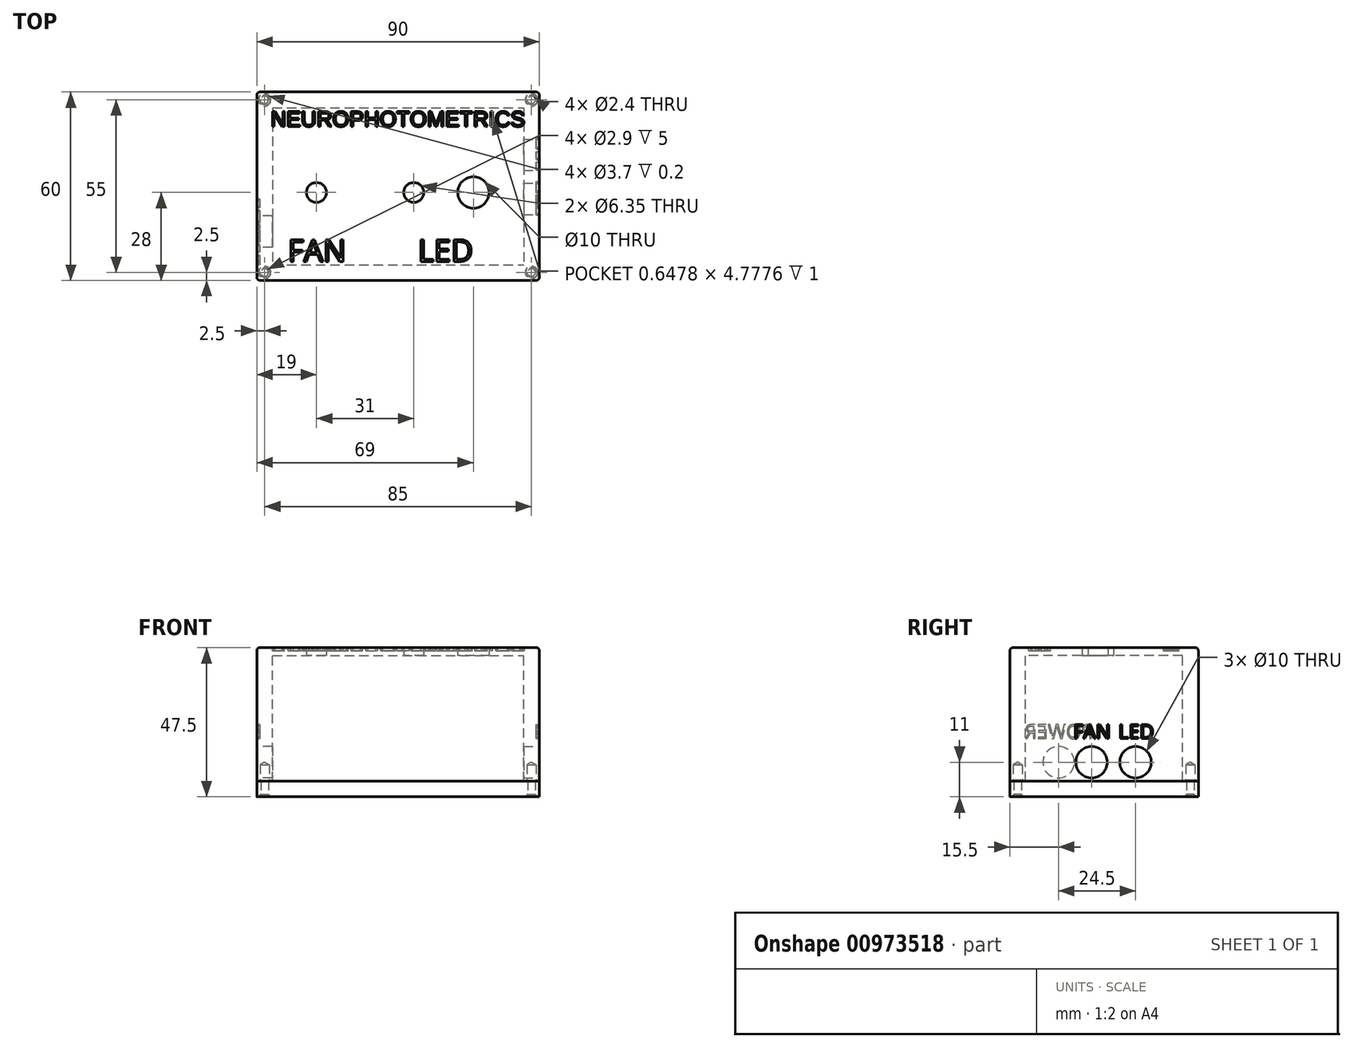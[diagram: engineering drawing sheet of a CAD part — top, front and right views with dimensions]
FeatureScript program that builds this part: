
annotation { "Feature Type Name" : "Feature", "Feature Type Description" : "" }
export const myFeature = defineFeature(function(context is Context, id is Id, definition is map)
    precondition{}
    {
        {
            var Q0;
            Q0=qCreatedBy(makeId("Top.planeOp"),FACE);
            var sketch = newSketch(context, id + "F0", { "sketchPlane" : qUnion([Q0])});
            skLineSegment(sketch, "E0.bottom", {"start": v(0, 0) * mm, "end": v(90, 0) * mm});
            skLineSegment(sketch, "E0.top", {"start": v(0, 60) * mm, "end": v(90, 60) * mm});
            skLineSegment(sketch, "E0.left", {"start": v(0, 0) * mm, "end": v(0, 60) * mm});
            skLineSegment(sketch, "E0.right", {"start": v(90, 0) * mm, "end": v(90, 60) * mm});
            skCircle(sketch, "E1", {"center": v(69, 28) * mm, "radius": 5 * mm});
            skCircle(sketch, "E2", {"center": v(19, 28) * mm, "radius": 3.18 * mm});
            skLineSegment(sketch, "E3", {"start": v(5, 60) * mm, "end": v(5, 5) * mm, "construction": true});
            skLineSegment(sketch, "E4", {"start": v(5, 5) * mm, "end": v(85, 5) * mm, "construction": true});
            skLineSegment(sketch, "E5", {"start": v(85, 5) * mm, "end": v(85, 60) * mm, "construction": true});
            skLineSegment(sketch, "E6", {"start": v(0, 55) * mm, "end": v(90, 55) * mm, "construction": true});
            skLineSegment(sketch, "E7", {"start": v(5, 5) * mm, "end": v(0, 5) * mm, "construction": true});
            skLineSegment(sketch, "E8", {"start": v(85, 5) * mm, "end": v(90, 5) * mm, "construction": true});
            skPoint(sketch, "E9.endSnap0", {"position": v(5, 32.5) * mm});
            skLineSegment(sketch, "E10", {"start": v(5, 60) * mm, "end": v(85, 55) * mm, "construction": true});
            skLineSegment(sketch, "E11", {"start": v(85, 60) * mm, "end": v(5, 55) * mm, "construction": true});
            skLineSegment(sketch, "E12", {"start": v(90, 5) * mm, "end": v(0, 0) * mm, "construction": true});
            skLineSegment(sketch, "E13", {"start": v(0, 5) * mm, "end": v(90, 0) * mm, "construction": true});
            skPoint(sketch, "E14", {"position": v(45, 2.5) * mm});
            skPoint(sketch, "E15", {"position": v(45, 57.5) * mm});
            skLineSegment(sketch, "E16", {"start": v(5, 28) * mm, "end": v(85, 28) * mm, "construction": true});
            skCircle(sketch, "E17", {"center": v(50, 28) * mm, "radius": 3.18 * mm});
            skSolve(sketch);
        }
        {
            var Q0;
            Q0=makeQuery(id+"F0.imprint","IMPRINT",FACE,{"disambiguationData":[TD([[makeQuery(id+"F0.imprint","IMPRINT",EDGE,{"derivedFrom":sQuery(id+"F0.wireOp",EDGE,"E0.bottom")}),1.0]])]});
            extrude(context, id + "F1", {"entities" : qUnion([Q0]), "depth" : 2.5 * mm, "offsetDistance" : 25 * mm});
        }
        {
            var Q0;
            Q0=makeQuery(id+"F1.opExtrude","CAP_FACE",FACE,{"disambiguationData":[OSD([sQuery(id+"F0.wireOp",EDGE,"E0.bottom"),sQuery(id+"F0.wireOp",EDGE,"E0.top"),sQuery(id+"F0.wireOp",EDGE,"E0.left"),sQuery(id+"F0.wireOp",EDGE,"E0.right"),sQuery(id+"F0.wireOp",EDGE,"692mbZP9-ke58-QfXx-eCDH-dWQCKjaEO8YG"),sQuery(id+"F0.wireOp",EDGE,"E1"),sQuery(id+"F0.wireOp",EDGE,"E2")])],"isStart":true});
            var sketch = newSketch(context, id + "F2", { "sketchPlane" : qUnion([Q0])});
            skLineSegment(sketch, "E18.bottom", {"start": v(0, -60) * mm, "end": v(90, -60) * mm, "construction": true});
            skLineSegment(sketch, "E18.top", {"start": v(0, 0) * mm, "end": v(90, 0) * mm, "construction": true});
            skLineSegment(sketch, "E18.left", {"start": v(0, -60) * mm, "end": v(0, 0) * mm, "construction": true});
            skLineSegment(sketch, "E18.right", {"start": v(90, -60) * mm, "end": v(90, 0) * mm, "construction": true});
            skLineSegment(sketch, "E19.bottom", {"start": v(5, -55) * mm, "end": v(85, -55) * mm});
            skLineSegment(sketch, "E19.top", {"start": v(5, -5) * mm, "end": v(85, -5) * mm});
            skLineSegment(sketch, "E19.left", {"start": v(5, -55) * mm, "end": v(5, -5) * mm});
            skLineSegment(sketch, "E19.right", {"start": v(85, -55) * mm, "end": v(85, -5) * mm});
            skSolve(sketch);
        }
        {
            var Q0;
            Q0=makeQuery(id+"F2.imprint","IMPRINT",FACE,{"disambiguationData":[TD([[makeQuery(id+"F2.imprint","IMPRINT",EDGE,{"derivedFrom":sQuery(id+"F2.wireOp",EDGE,"E19.bottom")}),-1.0]])]});
            var Q1;
            Q1=makeQuery(id+"F2.imprint","IMPRINT",FACE,{"disambiguationData":[TD([[makeQuery(id+"F2.imprint","IMPRINT",EDGE,{"derivedFrom":makeQuery(id+"FxvTJw6m9mzOm3c_1.hole-0.boolean.opBoolean","INTERSECT",EDGE,{"derivedFrom":[makeQuery(id+"F1.opExtrude","CAP_FACE",FACE,{"disambiguationData":[OSD([sQuery(id+"F0.wireOp",EDGE,"E0.bottom"),sQuery(id+"F0.wireOp",EDGE,"E0.top"),sQuery(id+"F0.wireOp",EDGE,"E0.left"),sQuery(id+"F0.wireOp",EDGE,"E0.right"),sQuery(id+"F0.wireOp",EDGE,"692mbZP9-ke58-QfXx-eCDH-dWQCKjaEO8YG"),sQuery(id+"F0.wireOp",EDGE,"E1"),sQuery(id+"F0.wireOp",EDGE,"E2")])],"isStart":true}),makeQuery(id+"FxvTJw6m9mzOm3c_1.hole-0.opRevolve","SWEPT_FACE",FACE,{"disambiguationData":[OSD([sQuery(id+"FxvTJw6m9mzOm3c_1.hole-0.sketch.wireOp",EDGE,"core_line_2")])]})]})}),1.0]])]});
            var Q2;
            Q2=makeQuery(id+"F2.imprint","IMPRINT",FACE,{"disambiguationData":[TD([[makeQuery(id+"F2.imprint","IMPRINT",EDGE,{"derivedFrom":makeQuery(id+"FxvTJw6m9mzOm3c_1.hole-1.boolean.opBoolean","INTERSECT",EDGE,{"derivedFrom":[makeQuery(id+"F1.opExtrude","CAP_FACE",FACE,{"disambiguationData":[OSD([sQuery(id+"F0.wireOp",EDGE,"E0.bottom"),sQuery(id+"F0.wireOp",EDGE,"E0.top"),sQuery(id+"F0.wireOp",EDGE,"E0.left"),sQuery(id+"F0.wireOp",EDGE,"E0.right"),sQuery(id+"F0.wireOp",EDGE,"692mbZP9-ke58-QfXx-eCDH-dWQCKjaEO8YG"),sQuery(id+"F0.wireOp",EDGE,"E1"),sQuery(id+"F0.wireOp",EDGE,"E2")])],"isStart":true}),makeQuery(id+"FxvTJw6m9mzOm3c_1.hole-1.opRevolve","SWEPT_FACE",FACE,{"disambiguationData":[OSD([sQuery(id+"FxvTJw6m9mzOm3c_1.hole-1.sketch.wireOp",EDGE,"core_line_2")])]})]})}),1.0]])]});
            var Q3;
            Q3=makeQuery(id+"F2.imprint","IMPRINT",FACE,{"disambiguationData":[TD([[makeQuery(id+"F2.imprint","IMPRINT",EDGE,{"derivedFrom":makeQuery(id+"FxvTJw6m9mzOm3c_1.hole-2.boolean.opBoolean","INTERSECT",EDGE,{"derivedFrom":[makeQuery(id+"F1.opExtrude","CAP_FACE",FACE,{"disambiguationData":[OSD([sQuery(id+"F0.wireOp",EDGE,"E0.bottom"),sQuery(id+"F0.wireOp",EDGE,"E0.top"),sQuery(id+"F0.wireOp",EDGE,"E0.left"),sQuery(id+"F0.wireOp",EDGE,"E0.right"),sQuery(id+"F0.wireOp",EDGE,"692mbZP9-ke58-QfXx-eCDH-dWQCKjaEO8YG"),sQuery(id+"F0.wireOp",EDGE,"E1"),sQuery(id+"F0.wireOp",EDGE,"E2")])],"isStart":true}),makeQuery(id+"FxvTJw6m9mzOm3c_1.hole-2.opRevolve","SWEPT_FACE",FACE,{"disambiguationData":[OSD([sQuery(id+"FxvTJw6m9mzOm3c_1.hole-2.sketch.wireOp",EDGE,"core_line_2")])]})]})}),1.0]])]});
            var Q4;
            Q4=makeQuery(id+"F2.imprint","IMPRINT",FACE,{"disambiguationData":[TD([[makeQuery(id+"F2.imprint","IMPRINT",EDGE,{"derivedFrom":makeQuery(id+"FxvTJw6m9mzOm3c_1.hole-3.boolean.opBoolean","INTERSECT",EDGE,{"derivedFrom":[makeQuery(id+"F1.opExtrude","CAP_FACE",FACE,{"disambiguationData":[OSD([sQuery(id+"F0.wireOp",EDGE,"E0.bottom"),sQuery(id+"F0.wireOp",EDGE,"E0.top"),sQuery(id+"F0.wireOp",EDGE,"E0.left"),sQuery(id+"F0.wireOp",EDGE,"E0.right"),sQuery(id+"F0.wireOp",EDGE,"692mbZP9-ke58-QfXx-eCDH-dWQCKjaEO8YG"),sQuery(id+"F0.wireOp",EDGE,"E1"),sQuery(id+"F0.wireOp",EDGE,"E2")])],"isStart":true}),makeQuery(id+"FxvTJw6m9mzOm3c_1.hole-3.opRevolve","SWEPT_FACE",FACE,{"disambiguationData":[OSD([sQuery(id+"FxvTJw6m9mzOm3c_1.hole-3.sketch.wireOp",EDGE,"core_line_2")])]})]})}),1.0]])]});
            extrude(context, id + "F3", {"entities" : qUnion([Q0, Q1, Q2, Q3, Q4]), "depth" : 40 * mm, "offsetDistance" : 25 * mm});
        }
        {
            var Q0;
            Q0=makeQuery(id+"F3.opExtrude","CAP_FACE",FACE,{"disambiguationData":[OSD([sQuery(id+"F0.wireOp",EDGE,"E0.bottom"),sQuery(id+"F0.wireOp",EDGE,"E0.top"),sQuery(id+"F0.wireOp",EDGE,"E0.left"),sQuery(id+"F0.wireOp",EDGE,"E0.right"),sQuery(id+"F2.wireOp",EDGE,"E19.bottom"),sQuery(id+"F2.wireOp",EDGE,"E19.top"),sQuery(id+"F2.wireOp",EDGE,"E19.left"),sQuery(id+"F2.wireOp",EDGE,"E19.right")])],"isStart":false});
            var sketch = newSketch(context, id + "F4", { "sketchPlane" : qUnion([Q0])});
            skLineSegment(sketch, "E20.bottom", {"start": v(0, 0) * mm, "end": v(90, 0) * mm});
            skLineSegment(sketch, "E20.top", {"start": v(0, -60) * mm, "end": v(90, -60) * mm});
            skLineSegment(sketch, "E20.left", {"start": v(0, 0) * mm, "end": v(0, -60) * mm});
            skLineSegment(sketch, "E20.right", {"start": v(90, 0) * mm, "end": v(90, -60) * mm});
            skLineSegment(sketch, "E21.bottom", {"start": v(5, -5) * mm, "end": v(85, -5) * mm, "construction": true});
            skLineSegment(sketch, "E21.top", {"start": v(5, -55) * mm, "end": v(85, -55) * mm, "construction": true});
            skLineSegment(sketch, "E21.left", {"start": v(5, -5) * mm, "end": v(5, -55) * mm, "construction": true});
            skLineSegment(sketch, "E21.right", {"start": v(85, -5) * mm, "end": v(85, -55) * mm, "construction": true});
            skSolve(sketch);
        }
        {
            var Q0;
            Q0=makeQuery(id+"F4.imprint","IMPRINT",FACE,{"disambiguationData":[TD([[makeQuery(id+"F4.imprint","IMPRINT",EDGE,{"derivedFrom":sQuery(id+"F4.wireOp",EDGE,"E20.bottom")}),-1.0]])]});
            var Q1;
            Q1=makeQuery(id+"F4.imprint","IMPRINT",FACE,{"disambiguationData":[TD([[makeQuery(id+"F4.imprint","IMPRINT",EDGE,{"derivedFrom":makeQuery(id+"F3.opExtrude","CAP_EDGE",EDGE,{"disambiguationData":[OSD([sQuery(id+"F2.wireOp",EDGE,"E19.bottom")])],"isStart":false})}),1.0]])]});
            extrude(context, id + "F5", {"entities" : qUnion([Q0, Q1]), "depth" : 5 * mm, "offsetDistance" : 25 * mm});
        }
        {
            var Q0;
            Q0=makeQuery(id+"F5.opExtrude","CAP_FACE",FACE,{"disambiguationData":[OSD([sQuery(id+"F4.wireOp",EDGE,"E20.bottom"),sQuery(id+"F4.wireOp",EDGE,"E20.top"),sQuery(id+"F4.wireOp",EDGE,"E20.left"),sQuery(id+"F4.wireOp",EDGE,"E20.right")])],"isStart":false});
            var sketch = newSketch(context, id + "F6", { "sketchPlane" : qUnion([Q0])});
            skLineSegment(sketch, "E22.bottom", {"start": v(0, -60) * mm, "end": v(90, -60) * mm, "construction": true});
            skLineSegment(sketch, "E22.top", {"start": v(0, 0) * mm, "end": v(90, 0) * mm, "construction": true});
            skLineSegment(sketch, "E22.left", {"start": v(0, -60) * mm, "end": v(0, 0) * mm, "construction": true});
            skLineSegment(sketch, "E22.right", {"start": v(90, -60) * mm, "end": v(90, 0) * mm, "construction": true});
            skLineSegment(sketch, "E23.bottom", {"start": v(5, -55) * mm, "end": v(85, -55) * mm, "construction": true});
            skLineSegment(sketch, "E23.top", {"start": v(5, -5) * mm, "end": v(85, -5) * mm, "construction": true});
            skLineSegment(sketch, "E23.left", {"start": v(5, -55) * mm, "end": v(5, -5) * mm, "construction": true});
            skLineSegment(sketch, "E23.right", {"start": v(85, -55) * mm, "end": v(85, -5) * mm, "construction": true});
            skLineSegment(sketch, "E24", {"start": v(5, -5) * mm, "end": v(0, 0) * mm, "construction": true});
            skLineSegment(sketch, "E25", {"start": v(85, -5) * mm, "end": v(90, 0) * mm, "construction": true});
            skLineSegment(sketch, "E26", {"start": v(85, -55) * mm, "end": v(90, -60) * mm, "construction": true});
            skLineSegment(sketch, "E27", {"start": v(5, -55) * mm, "end": v(0, -60) * mm, "construction": true});
            skPoint(sketch, "E28", {"position": v(2.5, -2.5) * mm});
            skPoint(sketch, "E29", {"position": v(87.5, -2.5) * mm});
            skPoint(sketch, "E30", {"position": v(87.5, -57.5) * mm});
            skPoint(sketch, "E31", {"position": v(2.5, -57.5) * mm});
            skSolve(sketch);
        }
        {
            var Q0;
            Q0=sQuery(id+"F6.wireOp",VERTEX,"E28");
            var Q1;
            Q1=sQuery(id+"F6.wireOp",VERTEX,"E31");
            var Q2;
            Q2=sQuery(id+"F6.wireOp",VERTEX,"E30");
            var Q3;
            Q3=sQuery(id+"F6.wireOp",VERTEX,"E29");
            var Q4;
            Q4=makeQuery(id+"F3.opExtrude","SWEPT_BODY",BODY,{"disambiguationData":[OSD([sQuery(id+"F0.wireOp",EDGE,"E0.bottom"),sQuery(id+"F0.wireOp",EDGE,"E0.top"),sQuery(id+"F0.wireOp",EDGE,"E0.left"),sQuery(id+"F0.wireOp",EDGE,"E0.right"),sQuery(id+"F2.wireOp",EDGE,"E19.bottom"),sQuery(id+"F2.wireOp",EDGE,"E19.top"),sQuery(id+"F2.wireOp",EDGE,"E19.left"),sQuery(id+"F2.wireOp",EDGE,"E19.right")])]});
            var Q5;
            Q5=makeQuery(id+"F5.opExtrude","SWEPT_BODY",BODY,{"disambiguationData":[OSD([sQuery(id+"F4.wireOp",EDGE,"E20.bottom"),sQuery(id+"F4.wireOp",EDGE,"E20.top"),sQuery(id+"F4.wireOp",EDGE,"E20.left"),sQuery(id+"F4.wireOp",EDGE,"E20.right")])]});
            hole(context, id + "F7", {"style" : HoleStyle.C_SINK, "endStyle" : HoleEndStyle.BLIND, "holeDiameter" : 2.4 * mm, "cSinkDiameter" : 4 * mm, "cSinkAngle" : 90 * degree, "majorDiameter" : 5 * mm, "holeDepth" : 5 * mm, "isTappedThrough" : true, "tappedDepth" : 12 * mm, "tapClearance" : 3, "locations" : qUnion([Q0, Q1, Q2, Q3]), "scope" : qUnion([Q4, Q5])});
        }
        {
            var Q0;
            Q0=makeQuery(id+"F3.opExtrude","CAP_FACE",FACE,{"disambiguationData":[OSD([sQuery(id+"F0.wireOp",EDGE,"E0.bottom"),sQuery(id+"F0.wireOp",EDGE,"E0.top"),sQuery(id+"F0.wireOp",EDGE,"E0.left"),sQuery(id+"F0.wireOp",EDGE,"E0.right"),sQuery(id+"F2.wireOp",EDGE,"E19.bottom"),sQuery(id+"F2.wireOp",EDGE,"E19.top"),sQuery(id+"F2.wireOp",EDGE,"E19.left"),sQuery(id+"F2.wireOp",EDGE,"E19.right")])],"isStart":false});
            var sketch = newSketch(context, id + "F8", { "sketchPlane" : qUnion([Q0])});
            skPoint(sketch, "E32", {"position": v(2.5, -2.5) * mm});
            skPoint(sketch, "E33", {"position": v(2.5, -57.5) * mm});
            skPoint(sketch, "E34", {"position": v(87.5, -57.5) * mm});
            skPoint(sketch, "E35", {"position": v(87.5, -2.5) * mm});
            skSolve(sketch);
        }
        {
            var Q0;
            Q0=sQuery(id+"F8.wireOp",VERTEX,"E32");
            var Q1;
            Q1=sQuery(id+"F8.wireOp",VERTEX,"E33");
            var Q2;
            Q2=sQuery(id+"F8.wireOp",VERTEX,"E34");
            var Q3;
            Q3=sQuery(id+"F8.wireOp",VERTEX,"E35");
            var Q4;
            Q4=makeQuery(id+"F3.opExtrude","SWEPT_BODY",BODY,{"disambiguationData":[OSD([sQuery(id+"F0.wireOp",EDGE,"E0.bottom"),sQuery(id+"F0.wireOp",EDGE,"E0.top"),sQuery(id+"F0.wireOp",EDGE,"E0.left"),sQuery(id+"F0.wireOp",EDGE,"E0.right"),sQuery(id+"F2.wireOp",EDGE,"E19.bottom"),sQuery(id+"F2.wireOp",EDGE,"E19.top"),sQuery(id+"F2.wireOp",EDGE,"E19.left"),sQuery(id+"F2.wireOp",EDGE,"E19.right")])]});
            hole(context, id + "F9", {"style" : HoleStyle.C_BORE, "endStyle" : HoleEndStyle.BLIND, "holeDiameter" : 2.9 * mm, "cBoreDiameter" : 3.7 * mm, "cBoreDepth" : .2 * mm, "majorDiameter" : 5 * mm, "holeDepth" : 5.2 * mm, "isTappedThrough" : true, "tappedDepth" : 12 * mm, "tapClearance" : 3, "locations" : qUnion([Q0, Q1, Q2, Q3]), "scope" : qUnion([Q4])});
        }
        {
            var Q0;
            Q0=makeQuery(id+"F1.opExtrude","CAP_EDGE",EDGE,{"disambiguationData":[OSD([sQuery(id+"F0.wireOp",EDGE,"E0.bottom")])],"isStart":false});
            var Q1;
            Q1=makeQuery(id+"F1.opExtrude","CAP_EDGE",EDGE,{"disambiguationData":[OSD([sQuery(id+"F0.wireOp",EDGE,"E0.left")])],"isStart":false});
            var Q2;
            Q2=makeQuery(id+"F1.opExtrude","CAP_EDGE",EDGE,{"disambiguationData":[OSD([sQuery(id+"F0.wireOp",EDGE,"E0.top")])],"isStart":false});
            var Q3;
            Q3=makeQuery(id+"F1.opExtrude","CAP_EDGE",EDGE,{"disambiguationData":[OSD([sQuery(id+"F0.wireOp",EDGE,"E0.right")])],"isStart":false});
            var Q4;
            Q4=makeQuery(id+"F3.opExtrude","SWEPT_EDGE",EDGE,{"disambiguationData":[OSD([sQuery(id+"F0.wireOp",EDGE,"E0.bottom"),sQuery(id+"F0.wireOp",EDGE,"E0.right")])]});
            var Q5;
            Q5=makeQuery(id+"F3.opExtrude","SWEPT_EDGE",EDGE,{"disambiguationData":[OSD([sQuery(id+"F0.wireOp",EDGE,"E0.bottom"),sQuery(id+"F0.wireOp",EDGE,"E0.left")])]});
            var Q6;
            Q6=makeQuery(id+"F1.opExtrude","SWEPT_EDGE",EDGE,{"disambiguationData":[OSD([sQuery(id+"F0.wireOp",EDGE,"E0.bottom"),sQuery(id+"F0.wireOp",EDGE,"E0.left")])]});
            var Q7;
            Q7=makeQuery(id+"F1.opExtrude","SWEPT_EDGE",EDGE,{"disambiguationData":[OSD([sQuery(id+"F0.wireOp",EDGE,"E0.bottom"),sQuery(id+"F0.wireOp",EDGE,"E0.right")])]});
            var Q8;
            Q8=makeQuery(id+"F3.opExtrude","SWEPT_EDGE",EDGE,{"disambiguationData":[OSD([sQuery(id+"F0.wireOp",EDGE,"E0.top"),sQuery(id+"F0.wireOp",EDGE,"E0.right")])]});
            var Q9;
            Q9=makeQuery(id+"F1.opExtrude","SWEPT_EDGE",EDGE,{"disambiguationData":[OSD([sQuery(id+"F0.wireOp",EDGE,"E0.top"),sQuery(id+"F0.wireOp",EDGE,"E0.right")])]});
            var Q10;
            Q10=makeQuery(id+"F3.opExtrude","SWEPT_EDGE",EDGE,{"disambiguationData":[OSD([sQuery(id+"F0.wireOp",EDGE,"E0.top"),sQuery(id+"F0.wireOp",EDGE,"E0.left")])]});
            var Q11;
            Q11=makeQuery(id+"F1.opExtrude","SWEPT_EDGE",EDGE,{"disambiguationData":[OSD([sQuery(id+"F0.wireOp",EDGE,"E0.top"),sQuery(id+"F0.wireOp",EDGE,"E0.left")])]});
            var Q12;
            Q12=makeQuery(id+"F5.opExtrude","SWEPT_EDGE",EDGE,{"disambiguationData":[OSD([sQuery(id+"F4.wireOp",EDGE,"E20.top"),sQuery(id+"F4.wireOp",EDGE,"E20.left")])]});
            var Q13;
            Q13=makeQuery(id+"F5.opExtrude","SWEPT_EDGE",EDGE,{"disambiguationData":[OSD([sQuery(id+"F4.wireOp",EDGE,"E20.bottom"),sQuery(id+"F4.wireOp",EDGE,"E20.left")])]});
            var Q14;
            Q14=makeQuery(id+"F5.opExtrude","SWEPT_EDGE",EDGE,{"disambiguationData":[OSD([sQuery(id+"F4.wireOp",EDGE,"E20.top"),sQuery(id+"F4.wireOp",EDGE,"E20.right")])]});
            var Q15;
            Q15=makeQuery(id+"F5.opExtrude","SWEPT_EDGE",EDGE,{"disambiguationData":[OSD([sQuery(id+"F4.wireOp",EDGE,"E20.bottom"),sQuery(id+"F4.wireOp",EDGE,"E20.right")])]});
            fillet(context, id + "F10", {"entities" : qUnion([Q0, Q1, Q2, Q3, Q4, Q5, Q6, Q7, Q8, Q9, Q10, Q11, Q12, Q13, Q14, Q15]), "radius" : 1 * mm, "tangentPropagation" : true, "allowEdgeOverflow" : false});
        }
        {
            var Q0;
            Q0=makeQuery(id+"F3.opExtrude","SWEPT_FACE",FACE,{"disambiguationData":[OSD([sQuery(id+"F0.wireOp",EDGE,"E0.left")])]});
            var sketch = newSketch(context, id + "F11", { "sketchPlane" : qUnion([Q0])});
            skCircle(sketch, "E36", {"center": v(-15.5, -34) * mm, "radius": 5 * mm});
            skLineSegment(sketch, "E37", {"start": v(-30, -40) * mm, "end": v(-30, 0) * mm, "construction": true});
            skLineSegment(sketch, "E38", {"start": v(-30, 0) * mm, "end": v(-1, -40) * mm, "construction": true});
            skLineSegment(sketch, "E39", {"start": v(-15.5, -20) * mm, "end": v(-15.5, -40) * mm, "construction": true});
            skLineSegment(sketch, "E40", {"start": v(-15.5, -40) * mm, "end": v(-15.5, 0) * mm, "construction": true});
            skSolve(sketch);
        }
        {
            var Q0;
            Q0=makeQuery(id+"F11.imprint","IMPRINT",FACE,{"disambiguationData":[TD([[makeQuery(id+"F11.imprint","IMPRINT",EDGE,{"derivedFrom":sQuery(id+"F11.wireOp",EDGE,"E36")}),1.0]])]});
            extrude(context, id + "F12", {"entities" : qUnion([Q0]), "operationType" : NewBodyOperationType.REMOVE, "endBound" : BoundingType.UP_TO_NEXT, "oppositeDirection" : true, "depth" : 25 * mm, "offsetDistance" : 25 * mm});
        }
        {
            var Q0;
            Q0=makeQuery(id+"F3.opExtrude","SWEPT_FACE",FACE,{"disambiguationData":[OSD([sQuery(id+"F0.wireOp",EDGE,"E0.right")])]});
            var sketch = newSketch(context, id + "F13", { "sketchPlane" : qUnion([Q0])});
            skLineSegment(sketch, "E41", {"start": v(1, -34) * mm, "end": v(59, -34) * mm, "construction": true});
            skCircle(sketch, "E42", {"center": v(26, -34) * mm, "radius": 5 * mm});
            skCircle(sketch, "E43", {"center": v(40, -34) * mm, "radius": 5 * mm});
            skSolve(sketch);
        }
        {
            var Q0;
            Q0=makeQuery(id+"F13.imprint","IMPRINT",FACE,{"disambiguationData":[TD([[makeQuery(id+"F13.imprint","IMPRINT",EDGE,{"derivedFrom":sQuery(id+"F13.wireOp",EDGE,"E42")}),1.0]])]});
            var Q1;
            Q1=makeQuery(id+"F13.imprint","IMPRINT",FACE,{"disambiguationData":[TD([[makeQuery(id+"F13.imprint","IMPRINT",EDGE,{"derivedFrom":sQuery(id+"F13.wireOp",EDGE,"E43")}),1.0]])]});
            var Q2;
            Q2=makeQuery(id+"F13.imprint","IMPRINT",FACE,{"disambiguationData":[TD([[makeQuery(id+"F13.imprint","IMPRINT",EDGE,{"derivedFrom":sQuery(id+"F13.wireOp",EDGE,"z5ahbYnX-TxnG-AjFd-NFLQ-6TXHqK5QM6zY")}),1.0]])]});
            extrude(context, id + "F14", {"entities" : qUnion([Q0, Q1, Q2]), "operationType" : NewBodyOperationType.REMOVE, "endBound" : BoundingType.UP_TO_NEXT, "oppositeDirection" : true, "depth" : 25 * mm, "offsetDistance" : 25 * mm});
        }
        {
            var Q0;
            Q0=makeQuery(id+"F10.opFillet","SPLIT",FACE,{"disambiguationData":[OD(4.0)],"derivedFrom":makeQuery(id+"F1.opExtrude","CAP_FACE",FACE,{"disambiguationData":[OSD([sQuery(id+"F0.wireOp",EDGE,"E0.bottom"),sQuery(id+"F0.wireOp",EDGE,"E0.top"),sQuery(id+"F0.wireOp",EDGE,"E0.left"),sQuery(id+"F0.wireOp",EDGE,"E0.right"),sQuery(id+"F0.wireOp",EDGE,"692mbZP9-ke58-QfXx-eCDH-dWQCKjaEO8YG"),sQuery(id+"F0.wireOp",EDGE,"E1"),sQuery(id+"F0.wireOp",EDGE,"E2")])],"isStart":false})});
            var sketch = newSketch(context, id + "F15", { "sketchPlane" : qUnion([Q0])});
            skLineSegment(sketch, "E44.bottom", {"start": v(1, 54) * mm, "end": v(89, 54) * mm, "construction": true});
            skLineSegment(sketch, "E44.top", {"start": v(1, 49) * mm, "end": v(89, 49) * mm, "construction": true});
            skLineSegment(sketch, "E44.left", {"start": v(1, 54) * mm, "end": v(1, 49) * mm, "construction": true});
            skLineSegment(sketch, "E44.right", {"start": v(89, 54) * mm, "end": v(89, 49) * mm, "construction": true});
            skLineSegment(sketch, "E45", {"start": v(45, 54) * mm, "end": v(45, 49) * mm, "construction": true});
            skLineSegment(sketch, "E46.bottom", {"start": v(76.58, 54) * mm, "end": v(4.4, 54) * mm, "construction": true});
            skLineSegment(sketch, "E46.top", {"start": v(85.6, 49) * mm, "end": v(13.42, 49) * mm, "construction": true});
            skLineSegment(sketch, "E46.left", {"start": v(76.58, 54) * mm, "end": v(85.6, 49) * mm, "construction": true});
            skLineSegment(sketch, "E46.right", {"start": v(4.4, 54) * mm, "end": v(13.42, 49) * mm, "construction": true});
            skPoint(sketch, "E46.middle", {"position": v(45, 51.5) * mm});
            skText(sketch, "E47", { "text": "NEUROPHOTOMETRICS\n", "fontName": "Arimo-Regular.ttf"});
            const initialGuessF15  = {"E47": [0.0044, 0.049, 1, 0, 0.005]};
            skSetInitialGuess(sketch, initialGuessF15);
            skSolve(sketch);
        }
        {
            var Q0;
            Q0=qSketchRegion(id+"F15",true);
            extrude(context, id + "F16", {"entities" : qUnion([Q0]), "operationType" : NewBodyOperationType.REMOVE, "oppositeDirection" : true, "depth" : 1 * mm, "offsetDistance" : 25 * mm});
        }
        {
            var Q0;
            Q0=makeQuery(id+"F3.opExtrude","SWEPT_BODY",BODY,{"disambiguationData":[OSD([sQuery(id+"F0.wireOp",EDGE,"E0.bottom"),sQuery(id+"F0.wireOp",EDGE,"E0.top"),sQuery(id+"F0.wireOp",EDGE,"E0.left"),sQuery(id+"F0.wireOp",EDGE,"E0.right"),sQuery(id+"F2.wireOp",EDGE,"E19.bottom"),sQuery(id+"F2.wireOp",EDGE,"E19.top"),sQuery(id+"F2.wireOp",EDGE,"E19.left"),sQuery(id+"F2.wireOp",EDGE,"E19.right")])]});
            var Q1;
            Q1=makeQuery(id+"F1.opExtrude","SWEPT_BODY",BODY,{"disambiguationData":[OSD([sQuery(id+"F0.wireOp",EDGE,"E0.bottom"),sQuery(id+"F0.wireOp",EDGE,"E0.top"),sQuery(id+"F0.wireOp",EDGE,"E0.left"),sQuery(id+"F0.wireOp",EDGE,"E0.right"),sQuery(id+"F0.wireOp",EDGE,"692mbZP9-ke58-QfXx-eCDH-dWQCKjaEO8YG"),sQuery(id+"F0.wireOp",EDGE,"E1"),sQuery(id+"F0.wireOp",EDGE,"E2")])]});
            booleanBodies(context, id + "F17", {"operationType" : BooleanOperationType.UNION, "tools" : qUnion([Q0, Q1])});
        }
        {
            var Q0;
            {var subQ0=sQuery(id+"F0.wireOp",EDGE,"E0.left");var subQ1=sQuery(id+"F0.wireOp",EDGE,"E0.top");var subQ2=sQuery(id+"F0.wireOp",EDGE,"E0.bottom");var subQ3=sQuery(id+"F0.wireOp",EDGE,"E0.right");var subQ4=sQuery(id+"F0.wireOp",EDGE,"E1");var subQ5=sQuery(id+"F0.wireOp",EDGE,"E2");Q0=makeQuery(id+"F16.boolean.opBoolean","SPLIT",FACE,{"disambiguationData":[TD([makeQuery(id+"F1.opExtrude","SWEPT_FACE",FACE,{"disambiguationData":[OSD([subQ4])]})])],"derivedFrom":makeQuery(id+"F1.opExtrude","CAP_FACE",FACE,{"disambiguationData":[OSD([subQ2,subQ1,subQ0,subQ3,subQ4,subQ5])],"isStart":false})});}
            var sketch = newSketch(context, id + "F18", { "sketchPlane" : qUnion([Q0])});
            skText(sketch, "E48", { "text": "FAN", "fontName": "OpenSans-Regular.ttf"});
            skText(sketch, "E49", { "text": "LED", "fontName": "OpenSans-Regular.ttf"});
            skLineSegment(sketch, "E50", {"start": v(19, 24.25) * mm, "end": v(19, 1) * mm, "construction": true});
            skLineSegment(sketch, "E51", {"start": v(59.75, 28) * mm, "end": v(59.75, 1) * mm, "construction": true});
            skPoint(sketch, "E52", {"position": v(19, 28) * mm});
            skLineSegment(sketch, "E53", {"start": v(59.75, 28) * mm, "end": v(50.5, 28) * mm, "construction": true});
            skPoint(sketch, "E54", {"position": v(59.75, 28) * mm});
            skLineSegment(sketch, "E55", {"start": v(59.75, 28) * mm, "end": v(59.75, 28) * mm});
            skLineSegment(sketch, "E56", {"start": v(50.5, 28) * mm, "end": v(69, 28) * mm, "construction": true});
            const initialGuessF18  = {"E48": [0.00991, 0.006, 1, 0, 0.007], "E49": [0.05134, 0.006, 1, 0, 0.007]};
            skSetInitialGuess(sketch, initialGuessF18);
            skSolve(sketch);
        }
        {
            var Q0;
            Q0 = qSketchRegion(id + "F18", true);
            extrude(context, id + "F19", {"entities" : qUnion([Q0]), "operationType" : NewBodyOperationType.REMOVE, "oppositeDirection" : true, "depth" : 1 * mm, "offsetDistance" : 25 * mm});
        }
        {
            var Q0;
            {var subQ0=sQuery(id+"F0.wireOp",EDGE,"E0.right");Q0=makeQuery(id+"F17.opBoolean","MERGE",FACE,{"derivedFrom":[makeQuery(id+"F1.opExtrude","SWEPT_FACE",FACE,{"disambiguationData":[OSD([subQ0])]}),makeQuery(id+"F3.opExtrude","SWEPT_FACE",FACE,{"disambiguationData":[OSD([subQ0])]})]});}
            var sketch = newSketch(context, id + "F20", { "sketchPlane" : qUnion([Q0])});
            skLineSegment(sketch, "E57", {"start": v(26, -34) * mm, "end": v(26, 0) * mm, "construction": true});
            skLineSegment(sketch, "E58", {"start": v(40, -34) * mm, "end": v(40, 0) * mm, "construction": true});
            skText(sketch, "E59", { "text": "FAN\n", "fontName": "OpenSans-Regular.ttf"});
            skText(sketch, "E60", { "text": "LED", "fontName": "OpenSans-Regular.ttf"});
            const initialGuessF20  = {"E59": [0.02016, -0.0265, 1, 0, 0.0045], "E60": [0.0346, -0.0265, 1, 0, 0.0045]};
            skSetInitialGuess(sketch, initialGuessF20);
            skSolve(sketch);
        }
        {
            var Q0;
            Q0 = qSketchRegion(id + "F20", true);
            extrude(context, id + "F21", {"entities" : qUnion([Q0]), "operationType" : NewBodyOperationType.REMOVE, "oppositeDirection" : true, "depth" : 1 * mm, "offsetDistance" : 25 * mm});
        }
        {
            var Q0;
            {var subQ0=sQuery(id+"F0.wireOp",EDGE,"E0.left");Q0=makeQuery(id+"F17.opBoolean","MERGE",FACE,{"derivedFrom":[makeQuery(id+"F1.opExtrude","SWEPT_FACE",FACE,{"disambiguationData":[OSD([subQ0])]}),makeQuery(id+"F3.opExtrude","SWEPT_FACE",FACE,{"disambiguationData":[OSD([subQ0])]})]});}
            var sketch = newSketch(context, id + "F22", { "sketchPlane" : qUnion([Q0])});
            skLineSegment(sketch, "E61", {"start": v(-15.5, -34) * mm, "end": v(-15.5, 1.5) * mm, "construction": true});
            skText(sketch, "E62", { "text": "POWER", "fontName": "OpenSans-Regular.ttf"});
            const initialGuessF22  = {"E62": [-0.02653, -0.0265, 1, 0, 0.0045]};
            skSetInitialGuess(sketch, initialGuessF22);
            skSolve(sketch);
        }
        {
            var Q0;
            Q0 = qSketchRegion(id + "F22", true);
            extrude(context, id + "F23", {"entities" : qUnion([Q0]), "operationType" : NewBodyOperationType.REMOVE, "oppositeDirection" : true, "depth" : 1 * mm, "offsetDistance" : 25 * mm});
        }
    });
